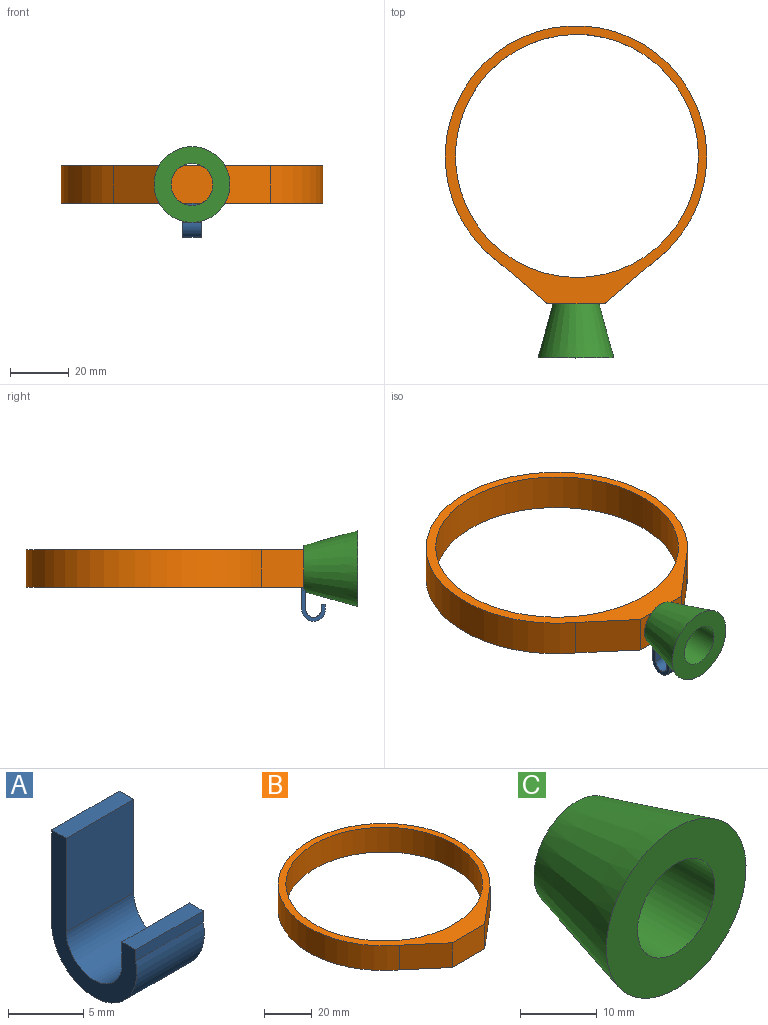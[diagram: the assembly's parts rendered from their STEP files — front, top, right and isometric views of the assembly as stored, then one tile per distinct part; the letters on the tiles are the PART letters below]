
ASSEMBLY  parts=3 mates=2
PART A: 10 faces, bbox 6.4x8x11.6 mm
  f0: plane 6.35x1.29mm, normal (0,0,1), area 8.2mm2, adj f1,f7,f8,f9
  f1: plane 6.35x0.9mm, normal (0,-1,0), area 5.7mm2, adj f0,f2,f8,f9
  f2: cylinder r=4mm len=8mm, axis (-1,0,0), area 85.6mm2, adj f1,f3,f8,f9
  f3: plane 7.62x6.35mm, normal (0,1,0), area 48.4mm2, adj f2,f4,f8,f9
  f4: plane 6.35x1.36mm, normal (0,0,1), area 8.7mm2, adj f3,f5,f8,f9
  f5: plane 7.62x6.35mm, normal (0,-1,0), area 48.4mm2, adj f4,f6,f8,f9
  f6: cylinder r=2.62mm len=6.35mm, axis (-1,0,0), area 52.3mm2, adj f5,f7,f8,f9
  f7: plane 6.35x1.81mm, normal (0,1,0), area 11.5mm2, adj f0,f6,f8,f9
  f8: plane 11.62x8mm, normal (1,0,0), area 27.1mm2, adj f0,f1,f2,f3,f4,f5,f6,f7
  f9: plane 11.62x8mm, normal (-1,0,0), area 27.1mm2, adj f0,f1,f2,f3,f4,f5,f6,f7
PART B: 7 faces, bbox 88.9x94.5x12.7 mm
  f0: cylinder r=44.45mm len=88.9mm, axis (0,0,-1), area 2824.8mm2, adj f1,f3,f5,f6
  f1: plane 16.86x14.37mm, normal (-0.65,-0.76,0), area 281.4mm2, adj f0,f2,f5,f6
  f2: plane 19.33x12.7mm, normal (0,-1,0), area 245.5mm2, adj f1,f3,f5,f6
  f3: plane 16.86x14.37mm, normal (0.65,-0.76,0), area 281.4mm2, adj f0,f2,f5,f6
  f4: cylinder r=41.27mm len=82.55mm, axis (0,0,-1), area 3293.6mm2, adj f5,f6
  f5: plane 94.48x88.9mm, normal (0,0,1), area 1057.7mm2, adj f0,f1,f2,f3,f4
  f6: plane 94.48x88.9mm, normal (0,0,-1), area 1057.7mm2, adj f0,f1,f2,f3,f4
PART C: 5 faces, bbox 25.8x18.4x25.8 mm
  f0: cone r=7.75mm half-angle=15.3deg, axis (0,1,0), area 109.3mm2, adj f2,f4
  f1: plane 25.79x25.79mm, normal (0,-1,0), area 362.4mm2, adj f3,f4
  f2: plane 15.76x15.76mm, normal (0,1,0), area 6.2mm2, adj f0,f3
  f3: cone r=12.9mm half-angle=15.3deg, axis (0,-1,0), area 1243.4mm2, adj f1,f2
  f4: cylinder r=7.14mm len=16.12mm, axis (0,-1,0), area 723.1mm2, adj f0,f1
PLACE A t=(14.89,-47.76,20.86)mm
PLACE B t=(18.07,-28.9,28.48)mm
PLACE C t=(18.07,-65.45,34.83)mm
MATE fastened A.f4 <-> B.f6  axis (0,0,1) through (18.07,-47.07,28.48)mm
MATE fastened C.f0 <-> B.f2  axis (0,1,0) through (18.07,-47.07,34.83)mm
